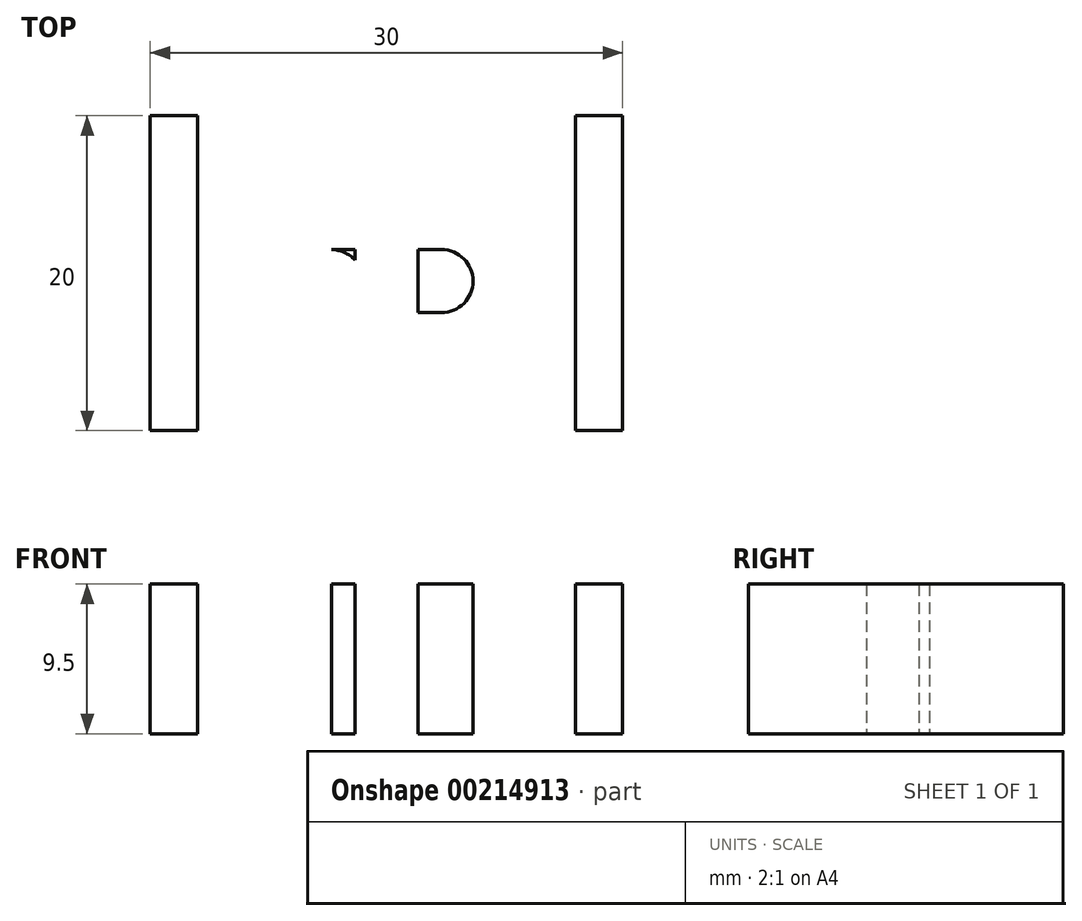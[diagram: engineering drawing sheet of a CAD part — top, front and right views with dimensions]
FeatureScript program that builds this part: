
annotation { "Feature Type Name" : "Feature", "Feature Type Description" : "" }
export const myFeature = defineFeature(function(context is Context, id is Id, definition is map)
    precondition{}
    {
        {
            var Q0;
            Q0=qCreatedBy(makeId("Top.planeOp"),FACE);
            var sketch = newSketch(context, id + "F0", { "sketchPlane" : qUnion([Q0])});
            skLineSegment(sketch, "E0", {"start": v(0, 0) * mm, "end": v(-30, 0) * mm});
            skLineSegment(sketch, "E1", {"start": v(-30, 0) * mm, "end": v(-30, 20) * mm});
            skLineSegment(sketch, "E2", {"start": v(-30, 20) * mm, "end": v(0, 20) * mm});
            skLineSegment(sketch, "E3", {"start": v(0, 20) * mm, "end": v(0, 0) * mm});
            skLineSegment(sketch, "E4", {"start": v(-15, 20) * mm, "end": v(-15, 11.15) * mm});
            skLineSegment(sketch, "E5", {"start": v(-15, 20) * mm, "end": v(-27, 20) * mm});
            skLineSegment(sketch, "E6", {"start": v(-27, 20) * mm, "end": v(-27, 0) * mm});
            skLineSegment(sketch, "E7", {"start": v(-15, 20) * mm, "end": v(-3, 20) * mm});
            skLineSegment(sketch, "E8", {"start": v(-3, 20) * mm, "end": v(-3, 0) * mm});
            skLineSegment(sketch, "E9", {"start": v(-11.5, 9.5) * mm, "end": v(-9.5, 9.5) * mm});
            skArc(sketch, "E10", {"start": v(-13, 8.18) * mm, "mid": v(-9.5, 9.5) * mm, "end": v(-13, 10.82) * mm});
            skLineSegment(sketch, "E11", {"start": v(-16.65, 9.5) * mm, "end": v(-17, 9.5) * mm});
            skArc(sketch, "E12", {"start": v(-17, 10.82) * mm, "mid": v(-20.32, 10.32) * mm, "end": v(-18.5, 7.5) * mm});
            skLineSegment(sketch, "E13", {"start": v(-18.5, 11.5) * mm, "end": v(-11.5, 11.5) * mm});
            skLineSegment(sketch, "E14", {"start": v(-11.5, 7.5) * mm, "end": v(-18.5, 7.5) * mm});
            skLineSegment(sketch, "E15", {"start": v(-17, 9.5) * mm, "end": v(-17, 7.5) * mm});
            skLineSegment(sketch, "E16", {"start": v(-17, 7.5) * mm, "end": v(-17, 11.5) * mm});
            skLineSegment(sketch, "E17.MirrorCS", {"start": v(-13, 7.5) * mm, "end": v(-13, 11.5) * mm});
            skSolve(sketch);
        }
        {
            var Q0;
            {var subQ0=sQuery(id+"F0.wireOp",EDGE,"E3");Q0=makeQuery(id+"F0.imprint","IMPRINT",FACE,{"disambiguationData":[TD([[makeQuery(id+"F0.imprint","IMPRINT",EDGE,{"derivedFrom":subQ0}),-1.0]])]});}
            var Q1;
            Q1=makeQuery(id+"F0.imprint","IMPRINT",FACE,{"disambiguationData":[TD([[makeQuery(id+"F0.imprint","IMPRINT",EDGE,{"derivedFrom":sQuery(id+"F0.wireOp",EDGE,"E5")}),1.0]])]});
            var Q2;
            {var subQ0=sQuery(id+"F0.wireOp",EDGE,"E1");Q2=makeQuery(id+"F0.imprint","IMPRINT",FACE,{"disambiguationData":[TD([[makeQuery(id+"F0.imprint","IMPRINT",EDGE,{"derivedFrom":subQ0}),-1.0]])]});}
            var Q3;
            {var subQ0=sQuery(id+"F0.wireOp",EDGE,"Oi5pEZMP-tZXi-ejHx-aOL7-sxTia0RvIkxy");Q3=makeQuery(id+"F0.imprint","IMPRINT",FACE,{"disambiguationData":[TD([[makeQuery(id+"F0.imprint","IMPRINT",EDGE,{"derivedFrom":subQ0}),1.0]])]});}
            var Q4;
            {var subQ1=sQuery(id+"F0.wireOp",EDGE,"E9");var subQ3=sQuery(id+"F0.wireOp",EDGE,"gUoS6kkO-rvrS-4EDR-Szo3-IT7tu6uQaZbb");var subQ4=makeQuery(id+"F0.imprint","INTERSECT",VERTEX,{"derivedFrom":[subQ1,subQ3]});Q4=makeQuery(id+"F0.imprint","IMPRINT",FACE,{"disambiguationData":[TD([[makeQuery(id+"F0.imprint","IMPRINT",EDGE,{"disambiguationData":[TD([[subQ4,1.0]])],"derivedFrom":subQ3}),-1.0]])]});}
            var Q5;
            {var subQ0=sQuery(id+"F0.wireOp",EDGE,"Oi5pEZMP-tZXi-ejHx-aOL7-sxTia0RvIkxy");Q5=makeQuery(id+"F0.imprint","IMPRINT",FACE,{"disambiguationData":[TD([[makeQuery(id+"F0.imprint","IMPRINT",EDGE,{"derivedFrom":subQ0}),-1.0]])]});}
            var Q6;
            {var subQ0=sQuery(id+"F0.wireOp",EDGE,"E13");var subQ1=sQuery(id+"F0.wireOp",EDGE,"E4");var subQ2=makeQuery(id+"F0.imprint","INTERSECT",VERTEX,{"derivedFrom":[subQ1,subQ0]});Q6=makeQuery(id+"F0.imprint","IMPRINT",FACE,{"disambiguationData":[TD([[makeQuery(id+"F0.imprint","IMPRINT",EDGE,{"disambiguationData":[TD([[subQ2,-1.0]])],"derivedFrom":subQ1}),1.0]])]});}
            var Q7;
            {var subQ0=sQuery(id+"F0.wireOp",EDGE,"E13");var subQ1=sQuery(id+"F0.wireOp",EDGE,"E4");var subQ2=makeQuery(id+"F0.imprint","INTERSECT",VERTEX,{"derivedFrom":[subQ1,subQ0]});Q7=makeQuery(id+"F0.imprint","IMPRINT",FACE,{"disambiguationData":[TD([[makeQuery(id+"F0.imprint","IMPRINT",EDGE,{"disambiguationData":[TD([[subQ2,-1.0]])],"derivedFrom":subQ1}),-1.0]])]});}
            var Q8;
            {var subQ0=sQuery(id+"F0.wireOp",EDGE,"erCPZfVF-JmHa-MoOo-ghoL-t5fRFZFRsmoJ");Q8=makeQuery(id+"F0.imprint","IMPRINT",FACE,{"disambiguationData":[TD([[makeQuery(id+"F0.imprint","IMPRINT",EDGE,{"derivedFrom":subQ0}),1.0]])]});}
            var Q9;
            {var subQ1=sQuery(id+"F0.wireOp",EDGE,"E9");var subQ5=sQuery(id+"F0.wireOp",EDGE,"E10");var subQ6=makeQuery(id+"F0.imprint","INTERSECT",VERTEX,{"derivedFrom":[subQ1,subQ5]});Q9=makeQuery(id+"F0.imprint","IMPRINT",FACE,{"disambiguationData":[TD([[makeQuery(id+"F0.imprint","IMPRINT",EDGE,{"disambiguationData":[TD([[subQ6,-1.0]])],"derivedFrom":subQ5}),-1.0]])]});}
            var Q10;
            {var subQ0=sQuery(id+"F0.wireOp",EDGE,"E14");Q10=makeQuery(id+"F0.imprint","IMPRINT",FACE,{"disambiguationData":[TD([[makeQuery(id+"F0.imprint","IMPRINT",EDGE,{"derivedFrom":subQ0}),-1.0]])]});}
            var Q11;
            {var subQ0=sQuery(id+"F0.wireOp",EDGE,"erCPZfVF-JmHa-MoOo-ghoL-t5fRFZFRsmoJ");Q11=makeQuery(id+"F0.imprint","IMPRINT",FACE,{"disambiguationData":[TD([[makeQuery(id+"F0.imprint","IMPRINT",EDGE,{"derivedFrom":subQ0}),-1.0]])]});}
            var Q12;
            {var subQ1=sQuery(id+"F0.wireOp",EDGE,"E9");var subQ3=sQuery(id+"F0.wireOp",EDGE,"gUoS6kkO-rvrS-4EDR-Szo3-IT7tu6uQaZbb");var subQ4=makeQuery(id+"F0.imprint","INTERSECT",VERTEX,{"derivedFrom":[subQ1,subQ3]});Q12=makeQuery(id+"F0.imprint","IMPRINT",FACE,{"disambiguationData":[TD([[makeQuery(id+"F0.imprint","IMPRINT",EDGE,{"disambiguationData":[TD([[subQ4,-1.0]])],"derivedFrom":subQ3}),-1.0]])]});}
            var Q13;
            {var subQ0=sQuery(id+"F0.wireOp",EDGE,"E9");var subQ5=sQuery(id+"F0.wireOp",EDGE,"E10");var subQ6=makeQuery(id+"F0.imprint","INTERSECT",VERTEX,{"derivedFrom":[subQ0,subQ5]});Q13=makeQuery(id+"F0.imprint","IMPRINT",FACE,{"disambiguationData":[TD([[makeQuery(id+"F0.imprint","IMPRINT",EDGE,{"disambiguationData":[TD([[subQ6,1.0]])],"derivedFrom":subQ5}),-1.0]])]});}
            var Q14;
            {var subQ0=sQuery(id+"F0.wireOp",EDGE,"E11");var subQ5=sQuery(id+"F0.wireOp",EDGE,"E12");var subQ6=makeQuery(id+"F0.imprint","INTERSECT",VERTEX,{"derivedFrom":[subQ0,subQ5]});Q14=makeQuery(id+"F0.imprint","IMPRINT",FACE,{"disambiguationData":[TD([[makeQuery(id+"F0.imprint","IMPRINT",EDGE,{"disambiguationData":[TD([[subQ6,-1.0]])],"derivedFrom":subQ5}),-1.0]])]});}
            var Q15;
            {var subQ0=sQuery(id+"F0.wireOp",EDGE,"E12");var subQ1=sQuery(id+"F0.wireOp",EDGE,"E11");var subQ2=makeQuery(id+"F0.imprint","INTERSECT",VERTEX,{"derivedFrom":[subQ1,subQ0]});Q15=makeQuery(id+"F0.imprint","IMPRINT",FACE,{"disambiguationData":[TD([[makeQuery(id+"F0.imprint","IMPRINT",EDGE,{"disambiguationData":[TD([[subQ2,-1.0]])],"derivedFrom":subQ1}),-1.0]])]});}
            var Q16;
            {var subQ0=sQuery(id+"F0.wireOp",EDGE,"E12");var subQ1=sQuery(id+"F0.wireOp",EDGE,"E11");var subQ2=makeQuery(id+"F0.imprint","INTERSECT",VERTEX,{"derivedFrom":[subQ1,subQ0]});Q16=makeQuery(id+"F0.imprint","IMPRINT",FACE,{"disambiguationData":[TD([[makeQuery(id+"F0.imprint","IMPRINT",EDGE,{"disambiguationData":[TD([[subQ2,-1.0]])],"derivedFrom":subQ1}),1.0]])]});}
            var Q17;
            {var subQ0=sQuery(id+"F0.wireOp",EDGE,"E10");var subQ1=sQuery(id+"F0.wireOp",EDGE,"E9");var subQ2=makeQuery(id+"F0.imprint","INTERSECT",VERTEX,{"derivedFrom":[subQ1,subQ0]});Q17=makeQuery(id+"F0.imprint","IMPRINT",FACE,{"disambiguationData":[TD([[makeQuery(id+"F0.imprint","IMPRINT",EDGE,{"disambiguationData":[TD([[subQ2,-1.0]])],"derivedFrom":subQ1}),-1.0]])]});}
            var Q18;
            {var subQ0=sQuery(id+"F0.wireOp",EDGE,"E10");var subQ1=sQuery(id+"F0.wireOp",EDGE,"E9");var subQ2=makeQuery(id+"F0.imprint","INTERSECT",VERTEX,{"derivedFrom":[subQ1,subQ0]});Q18=makeQuery(id+"F0.imprint","IMPRINT",FACE,{"disambiguationData":[TD([[makeQuery(id+"F0.imprint","IMPRINT",EDGE,{"disambiguationData":[TD([[subQ2,-1.0]])],"derivedFrom":subQ1}),1.0]])]});}
            var Q19;
            {var subQ0=sQuery(id+"F0.wireOp",EDGE,"E16");var subQ1=makeQuery(id+"F0.imprint","IMPRINT",VERTEX,{"derivedFrom":subQ0});Q19=makeQuery(id+"F0.imprint","IMPRINT",FACE,{"disambiguationData":[TD([[makeQuery(id+"F0.imprint","IMPRINT",EDGE,{"disambiguationData":[TD([[subQ1,1.0]])],"derivedFrom":subQ0}),1.0]])]});}
            var Q20;
            {var subQ1=sQuery(id+"F0.wireOp",EDGE,"E10");var subQ4=makeQuery(id+"F0.imprint","IMPRINT",VERTEX,{"derivedFrom":subQ1});Q20=makeQuery(id+"F0.imprint","IMPRINT",FACE,{"disambiguationData":[TD([[makeQuery(id+"F0.imprint","IMPRINT",EDGE,{"disambiguationData":[TD([[subQ4,1.0]])],"derivedFrom":subQ1}),1.0]])]});}
            extrude(context, id + "F1", {"entities" : qUnion([Q0, Q1, Q2, Q3, Q4, Q5, Q6, Q7, Q8, Q9, Q10, Q11, Q12, Q13, Q14, Q15, Q16, Q17, Q18, Q19, Q20]), "depth" : 6.5 * mm});
        }
        {
            var Q0;
            {var subQ0=sQuery(id+"F0.wireOp",EDGE,"Oi5pEZMP-tZXi-ejHx-aOL7-sxTia0RvIkxy");Q0=makeQuery(id+"F0.imprint","IMPRINT",FACE,{"disambiguationData":[TD([[makeQuery(id+"F0.imprint","IMPRINT",EDGE,{"derivedFrom":subQ0}),-1.0]])]});}
            var Q1;
            {var subQ0=sQuery(id+"F0.wireOp",EDGE,"Oi5pEZMP-tZXi-ejHx-aOL7-sxTia0RvIkxy");Q1=makeQuery(id+"F0.imprint","IMPRINT",FACE,{"disambiguationData":[TD([[makeQuery(id+"F0.imprint","IMPRINT",EDGE,{"derivedFrom":subQ0}),1.0]])]});}
            var Q2;
            {var subQ1=sQuery(id+"F0.wireOp",EDGE,"E9");var subQ3=sQuery(id+"F0.wireOp",EDGE,"gUoS6kkO-rvrS-4EDR-Szo3-IT7tu6uQaZbb");var subQ4=makeQuery(id+"F0.imprint","INTERSECT",VERTEX,{"derivedFrom":[subQ1,subQ3]});Q2=makeQuery(id+"F0.imprint","IMPRINT",FACE,{"disambiguationData":[TD([[makeQuery(id+"F0.imprint","IMPRINT",EDGE,{"disambiguationData":[TD([[subQ4,1.0]])],"derivedFrom":subQ3}),-1.0]])]});}
            var Q3;
            {var subQ1=sQuery(id+"F0.wireOp",EDGE,"E9");var subQ3=sQuery(id+"F0.wireOp",EDGE,"gUoS6kkO-rvrS-4EDR-Szo3-IT7tu6uQaZbb");var subQ4=makeQuery(id+"F0.imprint","INTERSECT",VERTEX,{"derivedFrom":[subQ1,subQ3]});Q3=makeQuery(id+"F0.imprint","IMPRINT",FACE,{"disambiguationData":[TD([[makeQuery(id+"F0.imprint","IMPRINT",EDGE,{"disambiguationData":[TD([[subQ4,-1.0]])],"derivedFrom":subQ3}),-1.0]])]});}
            var Q4;
            {var subQ0=sQuery(id+"F0.wireOp",EDGE,"erCPZfVF-JmHa-MoOo-ghoL-t5fRFZFRsmoJ");Q4=makeQuery(id+"F0.imprint","IMPRINT",FACE,{"disambiguationData":[TD([[makeQuery(id+"F0.imprint","IMPRINT",EDGE,{"derivedFrom":subQ0}),1.0]])]});}
            var Q5;
            {var subQ0=sQuery(id+"F0.wireOp",EDGE,"erCPZfVF-JmHa-MoOo-ghoL-t5fRFZFRsmoJ");Q5=makeQuery(id+"F0.imprint","IMPRINT",FACE,{"disambiguationData":[TD([[makeQuery(id+"F0.imprint","IMPRINT",EDGE,{"derivedFrom":subQ0}),-1.0]])]});}
            var Q6;
            {var subQ0=sQuery(id+"F0.wireOp",EDGE,"E13");var subQ1=sQuery(id+"F0.wireOp",EDGE,"E4");var subQ2=makeQuery(id+"F0.imprint","INTERSECT",VERTEX,{"derivedFrom":[subQ1,subQ0]});Q6=makeQuery(id+"F0.imprint","IMPRINT",FACE,{"disambiguationData":[TD([[makeQuery(id+"F0.imprint","IMPRINT",EDGE,{"disambiguationData":[TD([[subQ2,-1.0]])],"derivedFrom":subQ1}),-1.0]])]});}
            var Q7;
            {var subQ0=sQuery(id+"F0.wireOp",EDGE,"E13");var subQ1=sQuery(id+"F0.wireOp",EDGE,"E4");var subQ2=makeQuery(id+"F0.imprint","INTERSECT",VERTEX,{"derivedFrom":[subQ1,subQ0]});Q7=makeQuery(id+"F0.imprint","IMPRINT",FACE,{"disambiguationData":[TD([[makeQuery(id+"F0.imprint","IMPRINT",EDGE,{"disambiguationData":[TD([[subQ2,-1.0]])],"derivedFrom":subQ1}),1.0]])]});}
            var Q8;
            {var subQ1=sQuery(id+"F0.wireOp",EDGE,"E9");var subQ5=sQuery(id+"F0.wireOp",EDGE,"E10");var subQ6=makeQuery(id+"F0.imprint","INTERSECT",VERTEX,{"derivedFrom":[subQ1,subQ5]});Q8=makeQuery(id+"F0.imprint","IMPRINT",FACE,{"disambiguationData":[TD([[makeQuery(id+"F0.imprint","IMPRINT",EDGE,{"disambiguationData":[TD([[subQ6,-1.0]])],"derivedFrom":subQ5}),-1.0]])]});}
            var Q9;
            {var subQ0=sQuery(id+"F0.wireOp",EDGE,"E9");var subQ5=sQuery(id+"F0.wireOp",EDGE,"E10");var subQ6=makeQuery(id+"F0.imprint","INTERSECT",VERTEX,{"derivedFrom":[subQ0,subQ5]});Q9=makeQuery(id+"F0.imprint","IMPRINT",FACE,{"disambiguationData":[TD([[makeQuery(id+"F0.imprint","IMPRINT",EDGE,{"disambiguationData":[TD([[subQ6,1.0]])],"derivedFrom":subQ5}),-1.0]])]});}
            var Q10;
            {var subQ0=sQuery(id+"F0.wireOp",EDGE,"E11");var subQ5=sQuery(id+"F0.wireOp",EDGE,"E12");var subQ6=makeQuery(id+"F0.imprint","INTERSECT",VERTEX,{"derivedFrom":[subQ0,subQ5]});Q10=makeQuery(id+"F0.imprint","IMPRINT",FACE,{"disambiguationData":[TD([[makeQuery(id+"F0.imprint","IMPRINT",EDGE,{"disambiguationData":[TD([[subQ6,-1.0]])],"derivedFrom":subQ5}),-1.0]])]});}
            var Q11;
            {var subQ0=sQuery(id+"F0.wireOp",EDGE,"E10");var subQ1=sQuery(id+"F0.wireOp",EDGE,"E9");var subQ2=makeQuery(id+"F0.imprint","INTERSECT",VERTEX,{"derivedFrom":[subQ1,subQ0]});Q11=makeQuery(id+"F0.imprint","IMPRINT",FACE,{"disambiguationData":[TD([[makeQuery(id+"F0.imprint","IMPRINT",EDGE,{"disambiguationData":[TD([[subQ2,-1.0]])],"derivedFrom":subQ1}),1.0]])]});}
            var Q12;
            {var subQ0=sQuery(id+"F0.wireOp",EDGE,"E10");var subQ1=sQuery(id+"F0.wireOp",EDGE,"E9");var subQ2=makeQuery(id+"F0.imprint","INTERSECT",VERTEX,{"derivedFrom":[subQ1,subQ0]});Q12=makeQuery(id+"F0.imprint","IMPRINT",FACE,{"disambiguationData":[TD([[makeQuery(id+"F0.imprint","IMPRINT",EDGE,{"disambiguationData":[TD([[subQ2,-1.0]])],"derivedFrom":subQ1}),-1.0]])]});}
            var Q13;
            {var subQ0=sQuery(id+"F0.wireOp",EDGE,"E14");Q13=makeQuery(id+"F0.imprint","IMPRINT",FACE,{"disambiguationData":[TD([[makeQuery(id+"F0.imprint","IMPRINT",EDGE,{"derivedFrom":subQ0}),-1.0]])]});}
            var Q14;
            {var subQ0=sQuery(id+"F0.wireOp",EDGE,"E12");var subQ1=sQuery(id+"F0.wireOp",EDGE,"E11");var subQ2=makeQuery(id+"F0.imprint","INTERSECT",VERTEX,{"derivedFrom":[subQ1,subQ0]});Q14=makeQuery(id+"F0.imprint","IMPRINT",FACE,{"disambiguationData":[TD([[makeQuery(id+"F0.imprint","IMPRINT",EDGE,{"disambiguationData":[TD([[subQ2,-1.0]])],"derivedFrom":subQ1}),1.0]])]});}
            var Q15;
            {var subQ0=sQuery(id+"F0.wireOp",EDGE,"E12");var subQ1=sQuery(id+"F0.wireOp",EDGE,"E11");var subQ2=makeQuery(id+"F0.imprint","INTERSECT",VERTEX,{"derivedFrom":[subQ1,subQ0]});Q15=makeQuery(id+"F0.imprint","IMPRINT",FACE,{"disambiguationData":[TD([[makeQuery(id+"F0.imprint","IMPRINT",EDGE,{"disambiguationData":[TD([[subQ2,-1.0]])],"derivedFrom":subQ1}),-1.0]])]});}
            var Q16;
            {var subQ0=sQuery(id+"F0.wireOp",EDGE,"E16");var subQ1=makeQuery(id+"F0.imprint","IMPRINT",VERTEX,{"derivedFrom":subQ0});Q16=makeQuery(id+"F0.imprint","IMPRINT",FACE,{"disambiguationData":[TD([[makeQuery(id+"F0.imprint","IMPRINT",EDGE,{"disambiguationData":[TD([[subQ1,1.0]])],"derivedFrom":subQ0}),1.0]])]});}
            var Q17;
            {var subQ1=sQuery(id+"F0.wireOp",EDGE,"E10");var subQ4=makeQuery(id+"F0.imprint","IMPRINT",VERTEX,{"derivedFrom":subQ1});Q17=makeQuery(id+"F0.imprint","IMPRINT",FACE,{"disambiguationData":[TD([[makeQuery(id+"F0.imprint","IMPRINT",EDGE,{"disambiguationData":[TD([[subQ4,1.0]])],"derivedFrom":subQ1}),1.0]])]});}
            extrude(context, id + "F2", {"entities" : qUnion([Q0, Q1, Q2, Q3, Q4, Q5, Q6, Q7, Q8, Q9, Q10, Q11, Q12, Q13, Q14, Q15, Q16, Q17]), "operationType" : NewBodyOperationType.ADD, "oppositeDirection" : true, "depth" : 3 * mm});
        }
        {
            var Q0;
            {var subQ0=sQuery(id+"F0.wireOp",EDGE,"E1");Q0=makeQuery(id+"F0.imprint","IMPRINT",FACE,{"disambiguationData":[TD([[makeQuery(id+"F0.imprint","IMPRINT",EDGE,{"derivedFrom":subQ0}),-1.0]])]});}
            var Q1;
            {var subQ0=sQuery(id+"F0.wireOp",EDGE,"E3");Q1=makeQuery(id+"F0.imprint","IMPRINT",FACE,{"disambiguationData":[TD([[makeQuery(id+"F0.imprint","IMPRINT",EDGE,{"derivedFrom":subQ0}),-1.0]])]});}
            extrude(context, id + "F3", {"entities" : qUnion([Q0, Q1]), "operationType" : NewBodyOperationType.ADD, "oppositeDirection" : true, "depth" : 3 * mm});
        }
    });
